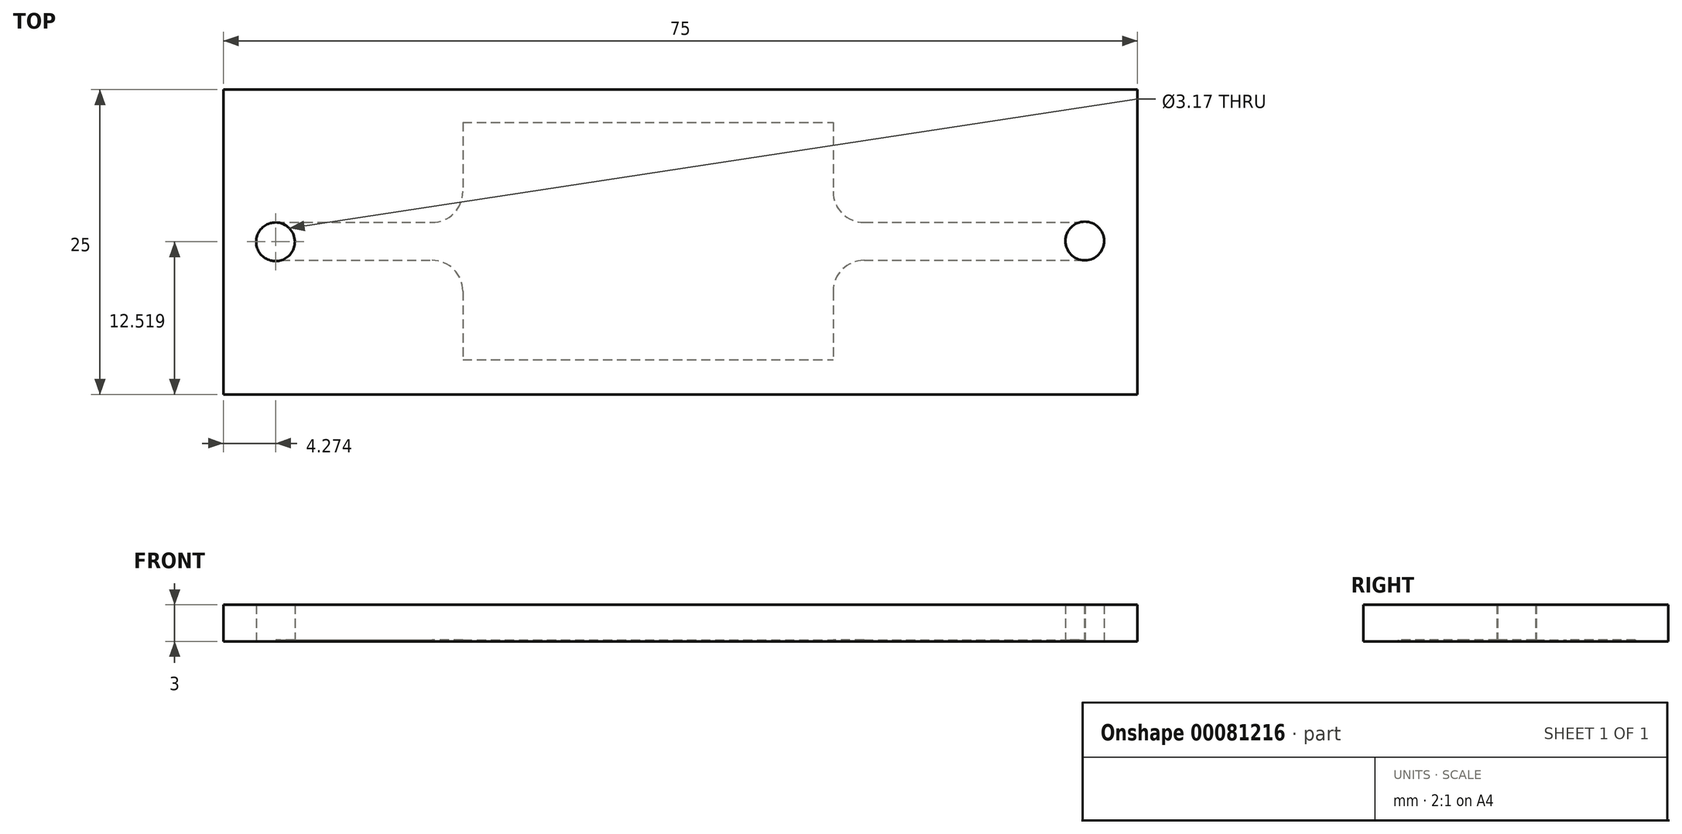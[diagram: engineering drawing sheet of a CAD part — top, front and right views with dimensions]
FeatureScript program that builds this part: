
annotation { "Feature Type Name" : "Feature", "Feature Type Description" : "" }
export const myFeature = defineFeature(function(context is Context, id is Id, definition is map)
    precondition{}
    {
        {
            var Q0;
            Q0=qCreatedBy(makeId("Top.planeOp"),FACE);
            var sketch = newSketch(context, id + "F0", { "sketchPlane" : qUnion([Q0])});
            skLineSegment(sketch, "E0.bottom", {"start": v(40.16, -6.83) * mm, "end": v(-34.84, -6.83) * mm});
            skLineSegment(sketch, "E0.top", {"start": v(40.16, 18.17) * mm, "end": v(-34.84, 18.17) * mm});
            skLineSegment(sketch, "E0.left", {"start": v(40.16, -6.83) * mm, "end": v(40.16, 18.17) * mm});
            skLineSegment(sketch, "E0.right", {"start": v(-34.84, -6.83) * mm, "end": v(-34.84, 18.17) * mm});
            skLineSegment(sketch, "E1", {"start": v(-34.84, -6.83) * mm, "end": v(-34.84, 5.67) * mm});
            skLineSegment(sketch, "E2", {"start": v(-34.84, 5.67) * mm, "end": v(40.16, 5.67) * mm});
            skSolve(sketch);
        }
        {
            var Q0;
            Q0=makeQuery(id+"F0.imprint","IMPRINT",FACE,{"disambiguationData":[TD([[makeQuery(id+"F0.imprint","IMPRINT",EDGE,{"derivedFrom":sQuery(id+"F0.wireOp",EDGE,"E0.bottom")}),-1.0]])]});
            var sketch = newSketch(context, id + "F1", { "sketchPlane" : qUnion([Q0])});
            skCircle(sketch, "E3", {"center": v(35.84, 5.75) * mm, "radius": 1.59 * mm});
            skCircle(sketch, "E4", {"center": v(-30.57, 5.69) * mm, "radius": 1.59 * mm});
            skLineSegment(sketch, "E5.bottom", {"start": v(-30.56, 7.28) * mm, "end": v(35.88, 7.28) * mm});
            skLineSegment(sketch, "E5.top", {"start": v(-30.56, 4.16) * mm, "end": v(35.88, 4.16) * mm});
            skLineSegment(sketch, "E5.left", {"start": v(-30.56, 7.28) * mm, "end": v(-30.56, 4.16) * mm});
            skLineSegment(sketch, "E5.right", {"start": v(35.88, 7.28) * mm, "end": v(35.88, 4.16) * mm});
            skLineSegment(sketch, "E6.bottom", {"start": v(-15.2, 15.49) * mm, "end": v(15.2, 15.49) * mm});
            skLineSegment(sketch, "E6.top", {"start": v(-15.2, -3.99) * mm, "end": v(15.2, -3.99) * mm});
            skLineSegment(sketch, "E6.left", {"start": v(-15.2, 15.49) * mm, "end": v(-15.2, -3.99) * mm});
            skLineSegment(sketch, "E6.right", {"start": v(15.2, 15.49) * mm, "end": v(15.2, -3.99) * mm});
            skPoint(sketch, "E6.middle", {"position": v(0, 5.75) * mm});
            skSolve(sketch);
        }
        {
            var Q0;
            {var subQ0=sQuery(id+"F0.wireOp",EDGE,"E0.bottom");Q0=makeQuery(id+"F0.imprint","IMPRINT",FACE,{"disambiguationData":[TD([[makeQuery(id+"F0.imprint","IMPRINT",EDGE,{"derivedFrom":subQ0}),-1.0]])]});}
            var Q1;
            {var subQ0=sQuery(id+"F0.wireOp",EDGE,"E0.top");Q1=makeQuery(id+"F0.imprint","IMPRINT",FACE,{"disambiguationData":[TD([[makeQuery(id+"F0.imprint","IMPRINT",EDGE,{"derivedFrom":subQ0}),1.0]])]});}
            extrude(context, id + "F2", {"entities" : qUnion([Q0, Q1]), "depth" : 3 * mm});
        }
        {
            var Q0;
            {var subQ1=sQuery(id+"F1.wireOp",EDGE,"E4");var subQ3=makeQuery(id+"F0.imprint","IMPRINT",EDGE,{"derivedFrom":sQuery(id+"F0.wireOp",EDGE,"E2")});var subQ4=makeQuery(id+"F1.imprint","INTERSECT",VERTEX,{"disambiguationData":[OD(0.0)],"derivedFrom":[subQ3,subQ1]});Q0=makeQuery(id+"F1.imprint","IMPRINT",FACE,{"disambiguationData":[TD([[makeQuery(id+"F1.imprint","IMPRINT",EDGE,{"disambiguationData":[TD([[subQ4,-1.0]])],"derivedFrom":subQ3}),1.0]])]});}
            var Q1;
            {var subQ0=sQuery(id+"F1.wireOp",EDGE,"E5.top");var subQ1=sQuery(id+"F1.wireOp",EDGE,"E4");var subQ2=makeQuery(id+"F1.imprint","INTERSECT",VERTEX,{"derivedFrom":[subQ1,subQ0]});Q1=makeQuery(id+"F1.imprint","IMPRINT",FACE,{"disambiguationData":[TD([[makeQuery(id+"F1.imprint","IMPRINT",EDGE,{"disambiguationData":[TD([[subQ2,1.0]])],"derivedFrom":subQ1}),1.0]])]});}
            var Q2;
            {var subQ0=sQuery(id+"F1.wireOp",EDGE,"E5.top");var subQ1=sQuery(id+"F1.wireOp",EDGE,"E4");var subQ2=makeQuery(id+"F1.imprint","INTERSECT",VERTEX,{"derivedFrom":[subQ1,subQ0]});Q2=makeQuery(id+"F1.imprint","IMPRINT",FACE,{"disambiguationData":[TD([[makeQuery(id+"F1.imprint","IMPRINT",EDGE,{"disambiguationData":[TD([[subQ2,-1.0]])],"derivedFrom":subQ1}),1.0]])]});}
            var Q3;
            {var subQ0=sQuery(id+"F1.wireOp",EDGE,"e85cab8e-166c-4b5d-8382-3d215b1240e5");var subQ1=sQuery(id+"F1.wireOp",EDGE,"E4");var subQ2=makeQuery(id+"F1.imprint","INTERSECT",VERTEX,{"derivedFrom":[subQ1,subQ0]});Q3=makeQuery(id+"F1.imprint","IMPRINT",FACE,{"disambiguationData":[TD([[makeQuery(id+"F1.imprint","IMPRINT",EDGE,{"disambiguationData":[TD([[subQ2,1.0]])],"derivedFrom":subQ1}),1.0]])]});}
            var Q4;
            {var subQ0=sQuery(id+"F1.wireOp",EDGE,"E5.bottom");var subQ1=sQuery(id+"F1.wireOp",EDGE,"E3");var subQ2=makeQuery(id+"F1.imprint","INTERSECT",VERTEX,{"derivedFrom":[subQ1,subQ0]});Q4=makeQuery(id+"F1.imprint","IMPRINT",FACE,{"disambiguationData":[TD([[makeQuery(id+"F1.imprint","IMPRINT",EDGE,{"disambiguationData":[TD([[subQ2,-1.0]])],"derivedFrom":subQ1}),1.0]])]});}
            var Q5;
            {var subQ0=sQuery(id+"F1.wireOp",EDGE,"E5.top");var subQ1=sQuery(id+"F1.wireOp",EDGE,"E3");var subQ2=makeQuery(id+"F1.imprint","INTERSECT",VERTEX,{"derivedFrom":[subQ1,subQ0]});Q5=makeQuery(id+"F1.imprint","IMPRINT",FACE,{"disambiguationData":[TD([[makeQuery(id+"F1.imprint","IMPRINT",EDGE,{"disambiguationData":[TD([[subQ2,1.0]])],"derivedFrom":subQ1}),1.0]])]});}
            var Q6;
            {var subQ1=sQuery(id+"F1.wireOp",EDGE,"E3");var subQ3=makeQuery(id+"F0.imprint","IMPRINT",EDGE,{"derivedFrom":sQuery(id+"F0.wireOp",EDGE,"E2")});var subQ4=makeQuery(id+"F1.imprint","INTERSECT",VERTEX,{"disambiguationData":[OD(0.0)],"derivedFrom":[subQ3,subQ1]});Q6=makeQuery(id+"F1.imprint","IMPRINT",FACE,{"disambiguationData":[TD([[makeQuery(id+"F1.imprint","IMPRINT",EDGE,{"disambiguationData":[TD([[subQ4,1.0]])],"derivedFrom":subQ3}),-1.0]])]});}
            var Q7;
            {var subQ0=sQuery(id+"F1.wireOp",EDGE,"E5.bottom");var subQ1=sQuery(id+"F1.wireOp",EDGE,"E3");var subQ2=makeQuery(id+"F1.imprint","INTERSECT",VERTEX,{"derivedFrom":[subQ1,subQ0]});Q7=makeQuery(id+"F1.imprint","IMPRINT",FACE,{"disambiguationData":[TD([[makeQuery(id+"F1.imprint","IMPRINT",EDGE,{"disambiguationData":[TD([[subQ2,1.0]])],"derivedFrom":subQ1}),1.0]])]});}
            var Q8;
            {var subQ1=sQuery(id+"F1.wireOp",EDGE,"E4");var subQ3=makeQuery(id+"F0.imprint","IMPRINT",EDGE,{"derivedFrom":sQuery(id+"F0.wireOp",EDGE,"E2")});var subQ4=makeQuery(id+"F1.imprint","INTERSECT",VERTEX,{"disambiguationData":[OD(1.0)],"derivedFrom":[subQ3,subQ1]});Q8=makeQuery(id+"F1.imprint","IMPRINT",FACE,{"disambiguationData":[TD([[makeQuery(id+"F1.imprint","IMPRINT",EDGE,{"disambiguationData":[TD([[subQ4,1.0]])],"derivedFrom":subQ3}),1.0]])]});}
            extrude(context, id + "F3", {"entities" : qUnion([Q0, Q1, Q2, Q3, Q4, Q5, Q6, Q7, Q8]), "operationType" : NewBodyOperationType.REMOVE, "depth" : 25.4 * mm});
        }
        {
            var Q0;
            {var subQ1=sQuery(id+"F1.wireOp",EDGE,"E5.top");var subQ8=sQuery(id+"F1.wireOp",EDGE,"E4");var subQ9=makeQuery(id+"F1.imprint","INTERSECT",VERTEX,{"derivedFrom":[subQ8,subQ1]});Q0=makeQuery(id+"F1.imprint","IMPRINT",FACE,{"disambiguationData":[TD([[makeQuery(id+"F1.imprint","IMPRINT",EDGE,{"disambiguationData":[TD([[subQ9,-1.0]])],"derivedFrom":subQ8}),-1.0]])]});}
            var Q1;
            {var subQ0=sQuery(id+"F1.wireOp",EDGE,"e85cab8e-166c-4b5d-8382-3d215b1240e5");var subQ3=sQuery(id+"F1.wireOp",EDGE,"E4");var subQ4=makeQuery(id+"F1.imprint","INTERSECT",VERTEX,{"derivedFrom":[subQ3,subQ0]});Q1=makeQuery(id+"F1.imprint","IMPRINT",FACE,{"disambiguationData":[TD([[makeQuery(id+"F1.imprint","IMPRINT",EDGE,{"disambiguationData":[TD([[subQ4,1.0]])],"derivedFrom":subQ3}),-1.0]])]});}
            var Q2;
            {var subQ5=sQuery(id+"F1.wireOp",EDGE,"E6.top");Q2=makeQuery(id+"F1.imprint","IMPRINT",FACE,{"disambiguationData":[TD([[makeQuery(id+"F1.imprint","IMPRINT",EDGE,{"derivedFrom":subQ5}),1.0]])]});}
            var Q3;
            {var subQ5=sQuery(id+"F1.wireOp",EDGE,"E6.bottom");Q3=makeQuery(id+"F1.imprint","IMPRINT",FACE,{"disambiguationData":[TD([[makeQuery(id+"F1.imprint","IMPRINT",EDGE,{"derivedFrom":subQ5}),-1.0]])]});}
            var Q4;
            {var subQ1=sQuery(id+"F1.wireOp",EDGE,"E5.bottom");var subQ7=sQuery(id+"F1.wireOp",EDGE,"E3");var subQ8=makeQuery(id+"F1.imprint","INTERSECT",VERTEX,{"derivedFrom":[subQ7,subQ1]});Q4=makeQuery(id+"F1.imprint","IMPRINT",FACE,{"disambiguationData":[TD([[makeQuery(id+"F1.imprint","IMPRINT",EDGE,{"disambiguationData":[TD([[subQ8,-1.0]])],"derivedFrom":subQ7}),-1.0]])]});}
            var Q5;
            {var subQ1=sQuery(id+"F1.wireOp",EDGE,"E5.top");var subQ3=sQuery(id+"F1.wireOp",EDGE,"E3");var subQ4=makeQuery(id+"F1.imprint","INTERSECT",VERTEX,{"derivedFrom":[subQ3,subQ1]});Q5=makeQuery(id+"F1.imprint","IMPRINT",FACE,{"disambiguationData":[TD([[makeQuery(id+"F1.imprint","IMPRINT",EDGE,{"disambiguationData":[TD([[subQ4,1.0]])],"derivedFrom":subQ3}),-1.0]])]});}
            var Q6;
            {var subQ0=sQuery(id+"F1.wireOp",EDGE,"E6.left");var subQ1=sQuery(id+"F1.wireOp",EDGE,"E5.bottom");var subQ2=makeQuery(id+"F1.imprint","INTERSECT",VERTEX,{"derivedFrom":[subQ1,subQ0]});Q6=makeQuery(id+"F1.imprint","IMPRINT",FACE,{"disambiguationData":[TD([[makeQuery(id+"F1.imprint","IMPRINT",EDGE,{"disambiguationData":[TD([[subQ2,-1.0]])],"derivedFrom":subQ1}),-1.0]])]});}
            var Q7;
            {var subQ0=sQuery(id+"F1.wireOp",EDGE,"E6.left");var subQ1=sQuery(id+"F1.wireOp",EDGE,"E5.top");var subQ2=makeQuery(id+"F1.imprint","INTERSECT",VERTEX,{"derivedFrom":[subQ1,subQ0]});Q7=makeQuery(id+"F1.imprint","IMPRINT",FACE,{"disambiguationData":[TD([[makeQuery(id+"F1.imprint","IMPRINT",EDGE,{"disambiguationData":[TD([[subQ2,-1.0]])],"derivedFrom":subQ1}),1.0]])]});}
            var Q8;
            {var subQ0=sQuery(id+"F1.wireOp",EDGE,"f7442fb1-22eb-4b81-94ff-7a8b5c8a4ed30.MirrorCS");var subQ1=sQuery(id+"F1.wireOp",EDGE,"E5.top");var subQ2=makeQuery(id+"F1.imprint","INTERSECT",VERTEX,{"disambiguationData":[OD(0.0)],"derivedFrom":[subQ1,subQ0]});Q8=makeQuery(id+"F1.imprint","IMPRINT",FACE,{"disambiguationData":[TD([[makeQuery(id+"F1.imprint","IMPRINT",EDGE,{"disambiguationData":[TD([[subQ2,-1.0]])],"derivedFrom":subQ1}),1.0]])]});}
            var Q9;
            {var subQ0=sQuery(id+"F1.wireOp",EDGE,"9eba685b-acd6-4631-9a7d-23c258058f2e0.MirrorCS");var subQ1=sQuery(id+"F1.wireOp",EDGE,"E5.top");var subQ2=makeQuery(id+"F1.imprint","INTERSECT",VERTEX,{"disambiguationData":[OD(0.0)],"derivedFrom":[subQ1,subQ0]});Q9=makeQuery(id+"F1.imprint","IMPRINT",FACE,{"disambiguationData":[TD([[makeQuery(id+"F1.imprint","IMPRINT",EDGE,{"disambiguationData":[TD([[subQ2,-1.0]])],"derivedFrom":subQ1}),1.0]])]});}
            var Q10;
            {var subQ0=sQuery(id+"F1.wireOp",EDGE,"c3d708f8-f24b-45cc-bd9d-1248575bf3a40.MirrorCS");var subQ1=sQuery(id+"F1.wireOp",EDGE,"E5.bottom");var subQ2=makeQuery(id+"F1.imprint","INTERSECT",VERTEX,{"disambiguationData":[OD(0.0)],"derivedFrom":[subQ1,subQ0]});Q10=makeQuery(id+"F1.imprint","IMPRINT",FACE,{"disambiguationData":[TD([[makeQuery(id+"F1.imprint","IMPRINT",EDGE,{"disambiguationData":[TD([[subQ2,1.0]])],"derivedFrom":subQ1}),-1.0]])]});}
            extrude(context, id + "F4", {"entities" : qUnion([Q0, Q1, Q2, Q3, Q4, Q5, Q6, Q7, Q8, Q9, Q10]), "operationType" : NewBodyOperationType.REMOVE, "depth" : .100 * mm});
        }
        {
            var Q0;
            Q0=makeQuery(id+"F4.boolean.opBoolean","COPY",EDGE,{"derivedFrom":makeQuery(id+"F4.opExtrude","SWEPT_EDGE",EDGE,{"disambiguationData":[OSD([sQuery(id+"F1.wireOp",EDGE,"E5.top"),sQuery(id+"F1.wireOp",EDGE,"E6.left")])]})});
            var Q1;
            Q1=makeQuery(id+"F4.boolean.opBoolean","COPY",EDGE,{"derivedFrom":makeQuery(id+"F4.opExtrude","SWEPT_EDGE",EDGE,{"disambiguationData":[OSD([sQuery(id+"F1.wireOp",EDGE,"E5.bottom"),sQuery(id+"F1.wireOp",EDGE,"E6.left")])]})});
            var Q2;
            Q2=makeQuery(id+"F4.boolean.opBoolean","COPY",EDGE,{"derivedFrom":makeQuery(id+"F4.opExtrude","SWEPT_EDGE",EDGE,{"disambiguationData":[OSD([sQuery(id+"F1.wireOp",EDGE,"E5.top"),sQuery(id+"F1.wireOp",EDGE,"E6.right")])]})});
            var Q3;
            Q3=makeQuery(id+"F4.boolean.opBoolean","COPY",EDGE,{"derivedFrom":makeQuery(id+"F4.opExtrude","SWEPT_EDGE",EDGE,{"disambiguationData":[OSD([sQuery(id+"F1.wireOp",EDGE,"E5.bottom"),sQuery(id+"F1.wireOp",EDGE,"E6.right")])]})});
            fillet(context, id + "F5", {"entities" : qUnion([Q0, Q1, Q2, Q3]), "radius" : 2.54 * mm, "tangentPropagation" : true, "allowEdgeOverflow" : false});
        }
    });
